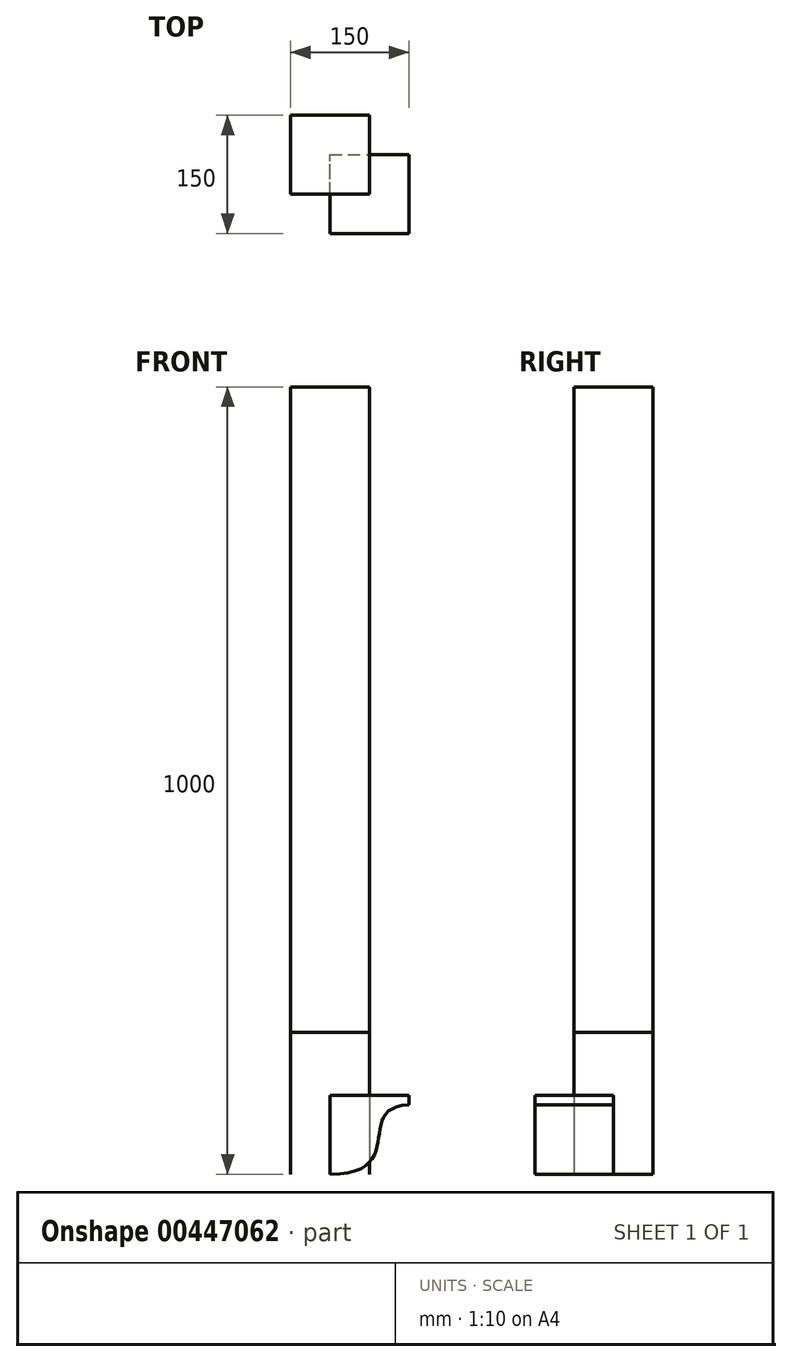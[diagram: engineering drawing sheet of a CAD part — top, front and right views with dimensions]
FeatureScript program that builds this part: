
annotation { "Feature Type Name" : "Feature", "Feature Type Description" : "" }
export const myFeature = defineFeature(function(context is Context, id is Id, definition is map)
    precondition{}
    {
        {
            var Q0;
            Q0=qCreatedBy(makeId("Top.planeOp"),FACE);
            var sketch = newSketch(context, id + "F0", { "sketchPlane" : qUnion([Q0])});
            skLineSegment(sketch, "E0.bottom", {"start": v(50, -50) * mm, "end": v(-50, -50) * mm});
            skLineSegment(sketch, "E0.top", {"start": v(50, 50) * mm, "end": v(-50, 50) * mm});
            skLineSegment(sketch, "E0.left", {"start": v(50, -50) * mm, "end": v(50, 50) * mm});
            skLineSegment(sketch, "E0.right", {"start": v(-50, -50) * mm, "end": v(-50, 50) * mm});
            skPoint(sketch, "E0.middle", {"position": v(0, 0) * mm});
            skSolve(sketch);
        }
        {
            var Q0;
            Q0=makeQuery(id+"F0.imprint","IMPRINT",FACE,{"disambiguationData":[TD([[makeQuery(id+"F0.imprint","IMPRINT",EDGE,{"derivedFrom":sQuery(id+"F0.wireOp",EDGE,"E0.bottom")}),-1.0]])]});
            extrude(context, id + "F1", {"entities" : qUnion([Q0]), "depth" : 1000 * mm, "offsetDistance" : 25 * mm});
        }
        {
            var Q0;
            Q0=makeQuery(id+"F0.imprint","IMPRINT",FACE,{"disambiguationData":[TD([[makeQuery(id+"F0.imprint","IMPRINT",EDGE,{"derivedFrom":sQuery(id+"F0.wireOp",EDGE,"E0.bottom")}),-1.0]])]});
            extrude(context, id + "F2", {"entities" : qUnion([Q0]), "depth" : 180 * mm, "offsetDistance" : 25 * mm});
        }
        {
            var Q0;
            Q0=qCreatedBy(makeId("Front.planeOp"),FACE);
            var sketch = newSketch(context, id + "F3", { "sketchPlane" : qUnion([Q0])});
            skLineSegment(sketch, "E1", {"start": v(0, 0) * mm, "end": v(0, 100) * mm});
            skLineSegment(sketch, "E2", {"start": v(0, 100) * mm, "end": v(100, 100) * mm});
            skLineSegment(sketch, "E3", {"start": v(100, 100) * mm, "end": v(100, 88) * mm});
            skPoint(sketch, "E4.1.internal.snap0", {"position": v(0, 50) * mm});
            skFitSpline(sketch, "E4", {"points": [v(0, 0) * mm, v(62.26, 50) * mm, v(100, 88) * mm], "startDerivative": vector(307.25, 0) * mm, "endDerivative": vector(210.65, 8.7) * mm});
            skSolve(sketch);
        }
        {
            var Q0;
            Q0=makeQuery(id+"F3.imprint","IMPRINT",FACE,{"disambiguationData":[TD([[makeQuery(id+"F3.imprint","IMPRINT",EDGE,{"derivedFrom":sQuery(id+"F3.wireOp",EDGE,"E1")}),-1.0]])]});
            extrude(context, id + "F4", {"entities" : qUnion([Q0]), "depth" : 100 * mm, "offsetDistance" : 25 * mm});
        }
    });
